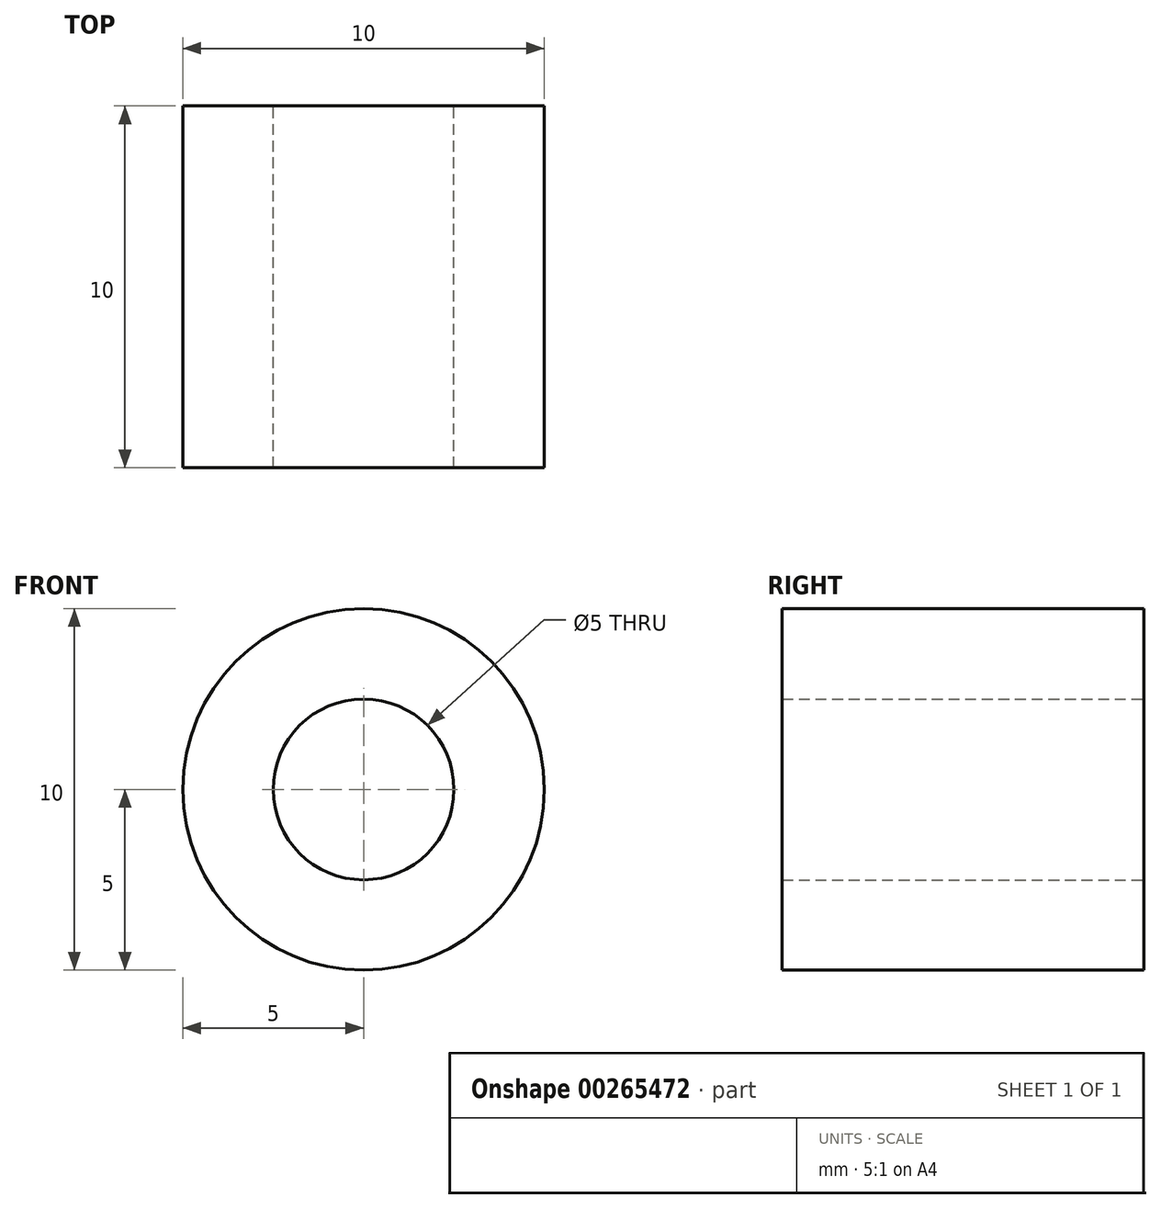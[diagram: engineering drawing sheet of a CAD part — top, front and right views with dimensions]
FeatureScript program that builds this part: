
annotation { "Feature Type Name" : "Feature", "Feature Type Description" : "" }
export const myFeature = defineFeature(function(context is Context, id is Id, definition is map)
    precondition{}
    {
        {
            var Q0;
            Q0=qCreatedBy(makeId("Front.planeOp"),FACE);
            var sketch = newSketch(context, id + "F0", { "sketchPlane" : qUnion([Q0])});
            skCircle(sketch, "E0", {"center": v(0, 0) * mm, "radius": 2.5 * mm});
            skCircle(sketch, "E1", {"center": v(0, 0) * mm, "radius": 5 * mm});
            skSolve(sketch);
        }
        {
            var Q0;
            Q0=makeQuery(id+"F0.imprint","IMPRINT",FACE,{"disambiguationData":[TD([[makeQuery(id+"F0.imprint","IMPRINT",EDGE,{"derivedFrom":sQuery(id+"F0.wireOp",EDGE,"E0")}),-1.0]])]});
            extrude(context, id + "F1", {"entities" : qUnion([Q0]), "depth" : 10 * mm});
        }
    });
